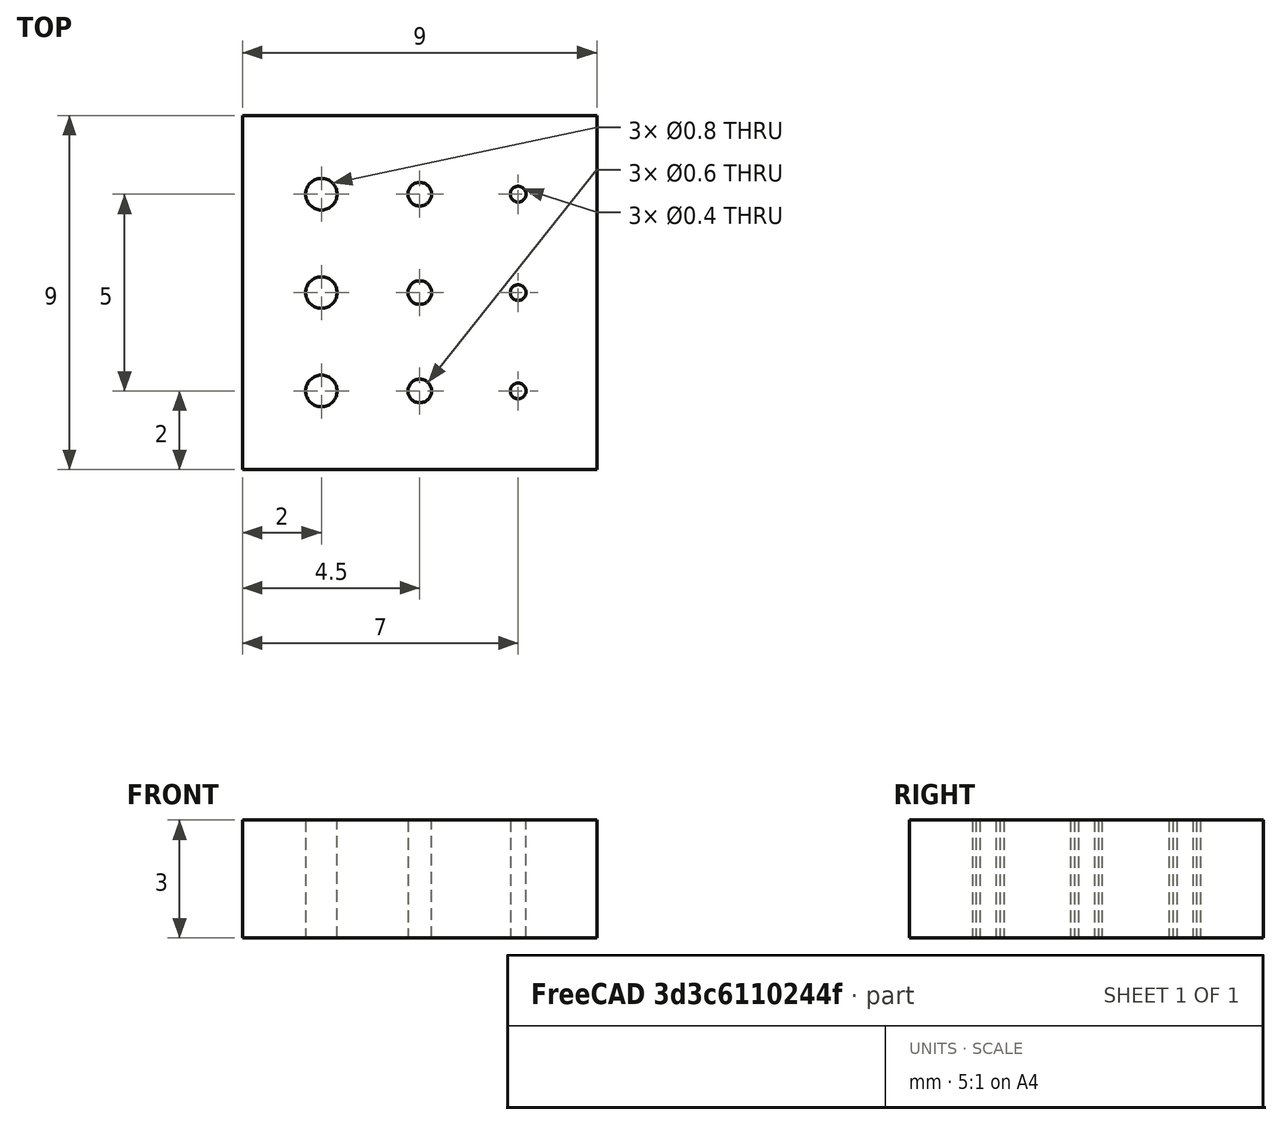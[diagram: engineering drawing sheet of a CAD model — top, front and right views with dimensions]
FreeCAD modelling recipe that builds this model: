
FCSTD DOCUMENT  (FreeCAD 0.17R13519 (Git))
Label: hole-test
License: All rights reserved
LicenseURL: http://en.wikipedia.org/wiki/All_rights_reserved
objects: Sketcher::SketchObject×1, PartDesign::Pad×1, PartDesign::Body×1
note: 4 computed .brp shape members not serialized (recipe doc carries the construction recipe); baked Part::Feature solids carry a one-line shape summary decoded from their .brp

FEATURE [Sketcher::SketchObject] Sketch
  MapMode = 5
  Support = -> [XY_Plane]
  sketch-geometry (26):
    g0: LineSegment StartX=0 StartY=0 StartZ=0 EndX=9 EndY=0 EndZ=0
    g1: LineSegment StartX=9 StartY=0 StartZ=0 EndX=9 EndY=9 EndZ=0
    g2: LineSegment StartX=9 StartY=9 StartZ=0 EndX=0 EndY=9 EndZ=0
    g3: Circle CenterX=2 CenterY=2 CenterZ=0 NormalX=0 NormalY=0 NormalZ=1 AngleXU=0 Radius=0.4
    g4: Circle CenterX=4.5 CenterY=2 CenterZ=0 NormalX=0 NormalY=0 NormalZ=1 AngleXU=0 Radius=0.3
    g5: Circle CenterX=7 CenterY=2 CenterZ=0 NormalX=0 NormalY=0 NormalZ=1 AngleXU=0 Radius=0.2
    g6: LineSegment [constr] StartX=2 StartY=2 StartZ=0 EndX=0 EndY=2 EndZ=0
    g7: LineSegment [constr] StartX=2 StartY=2 StartZ=0 EndX=4.5 EndY=2 EndZ=0
    g8: LineSegment [constr] StartX=4.5 StartY=2 StartZ=0 EndX=7 EndY=2 EndZ=0
    g9: LineSegment StartX=0 StartY=0 StartZ=0 EndX=0 EndY=2 EndZ=0
    g10: LineSegment [constr] StartX=7 StartY=2 StartZ=0 EndX=9 EndY=2 EndZ=0
    g11: Circle CenterX=2 CenterY=4.5 CenterZ=0 NormalX=0 NormalY=0 NormalZ=1 AngleXU=0 Radius=0.4
    g12: Circle CenterX=4.5 CenterY=4.5 CenterZ=0 NormalX=0 NormalY=0 NormalZ=1 AngleXU=0 Radius=0.3
    g13: Circle CenterX=7 CenterY=4.5 CenterZ=0 NormalX=0 NormalY=0 NormalZ=1 AngleXU=0 Radius=0.2
    g14: LineSegment [constr] StartX=2 StartY=4.5 StartZ=0 EndX=0 EndY=4.5 EndZ=0
    g15: LineSegment [constr] StartX=2 StartY=4.5 StartZ=0 EndX=4.5 EndY=4.5 EndZ=0
    g16: LineSegment [constr] StartX=4.5 StartY=4.5 StartZ=0 EndX=7 EndY=4.5 EndZ=0
    g17: LineSegment StartX=0 StartY=2 StartZ=0 EndX=0 EndY=4.5 EndZ=0
    g18: Circle CenterX=2 CenterY=7 CenterZ=0 NormalX=0 NormalY=0 NormalZ=1 AngleXU=0 Radius=0.4
    g19: Circle CenterX=4.5 CenterY=7 CenterZ=0 NormalX=0 NormalY=0 NormalZ=1 AngleXU=0 Radius=0.3
    g20: Circle CenterX=7 CenterY=7 CenterZ=0 NormalX=0 NormalY=0 NormalZ=1 AngleXU=0 Radius=0.2
    g21: LineSegment [constr] StartX=2 StartY=7 StartZ=0 EndX=0 EndY=7 EndZ=0
    g22: LineSegment [constr] StartX=2 StartY=7 StartZ=0 EndX=4.5 EndY=7 EndZ=0
    g23: LineSegment [constr] StartX=4.5 StartY=7 StartZ=0 EndX=7 EndY=7 EndZ=0
    g24: LineSegment StartX=0 StartY=4.5 StartZ=0 EndX=0 EndY=7 EndZ=0
    g25: LineSegment StartX=0 StartY=7 StartZ=0 EndX=0 EndY=9 EndZ=0
  constraints (68):
    c: Coincident(g0,g1)
    c: Coincident(g1,g2)
    c: Horizontal(g0)
    c: Horizontal(g2)
    c: Vertical(g1)
    c: Coincident(g0,g-1)
    c: Coincident(g6,g3)
    c: Horizontal(g6)
    c: Coincident(g7,g3)
    c: Coincident(g7,g4)
    c: Horizontal(g7)
    c: Coincident(g8,g4)
    c: Coincident(g8,g5)
    c: Horizontal(g8)
    c: Distance(g6) = 2
    c: Coincident(g9,g-1)
    c: Coincident(g9,g6)
    c: Vertical(g9)
    c: Equal(g9,g6)
    c: Distance(g7) = 2.5
    c: Equal(g8,g7)
    c: Coincident(g10,g5)
    c: PointOnObject(g10,g1)
    c: Horizontal(g10)
    c: Equal(g10,g6)
    c: Coincident(g14,g11)
    c: Horizontal(g14)
    c: Coincident(g15,g11)
    c: Coincident(g15,g12)
    c: Horizontal(g15)
    c: Coincident(g16,g12)
    c: Coincident(g16,g13)
    c: Horizontal(g16)
    c: Equal(g6,g14) = 2
    c: Equal(g7,g15) = 2.5
    c: Equal(g16,g15)
    c: Coincident(g17,g6)
    c: Coincident(g17,g14)
    c: Vertical(g17)
    c: Equal(g17,g7)
    c: Coincident(g21,g18)
    c: Horizontal(g21)
    c: Coincident(g22,g18)
    c: Coincident(g22,g19)
    c: Horizontal(g22)
    c: Coincident(g23,g19)
    c: Coincident(g23,g20)
    c: Horizontal(g23)
    c: Equal(g23,g22)
    c: Equal(g21,g14)
    c: Equal(g22,g15)
    c: Coincident(g24,g14)
    c: Coincident(g24,g21)
    c: Vertical(g24)
    c: Equal(g24,g17)
    c: Coincident(g25,g21)
    c: Coincident(g25,g2)
    c: Vertical(g25)
    c: Equal(g25,g9)
    c: Radius(g5) = 0.2
    c: Radius(g4) = 0.3
    c: Radius(g3) = 0.4
    c: Equal(g11,g3)
    c: Equal(g12,g4)
    c: Equal(g13,g5)
    c: Equal(g20,g13)
    c: Equal(g19,g12)
    c: Equal(g18,g11)
FEATURE [PartDesign::Pad] Pad
  Length = 3
  Length2 = 100
  Profile = -> Sketch
  Type = 0
FEATURE [PartDesign::Body] Body
  Group = -> [Sketch,Pad]
  Origin = -> Origin
  Tip = -> Pad
